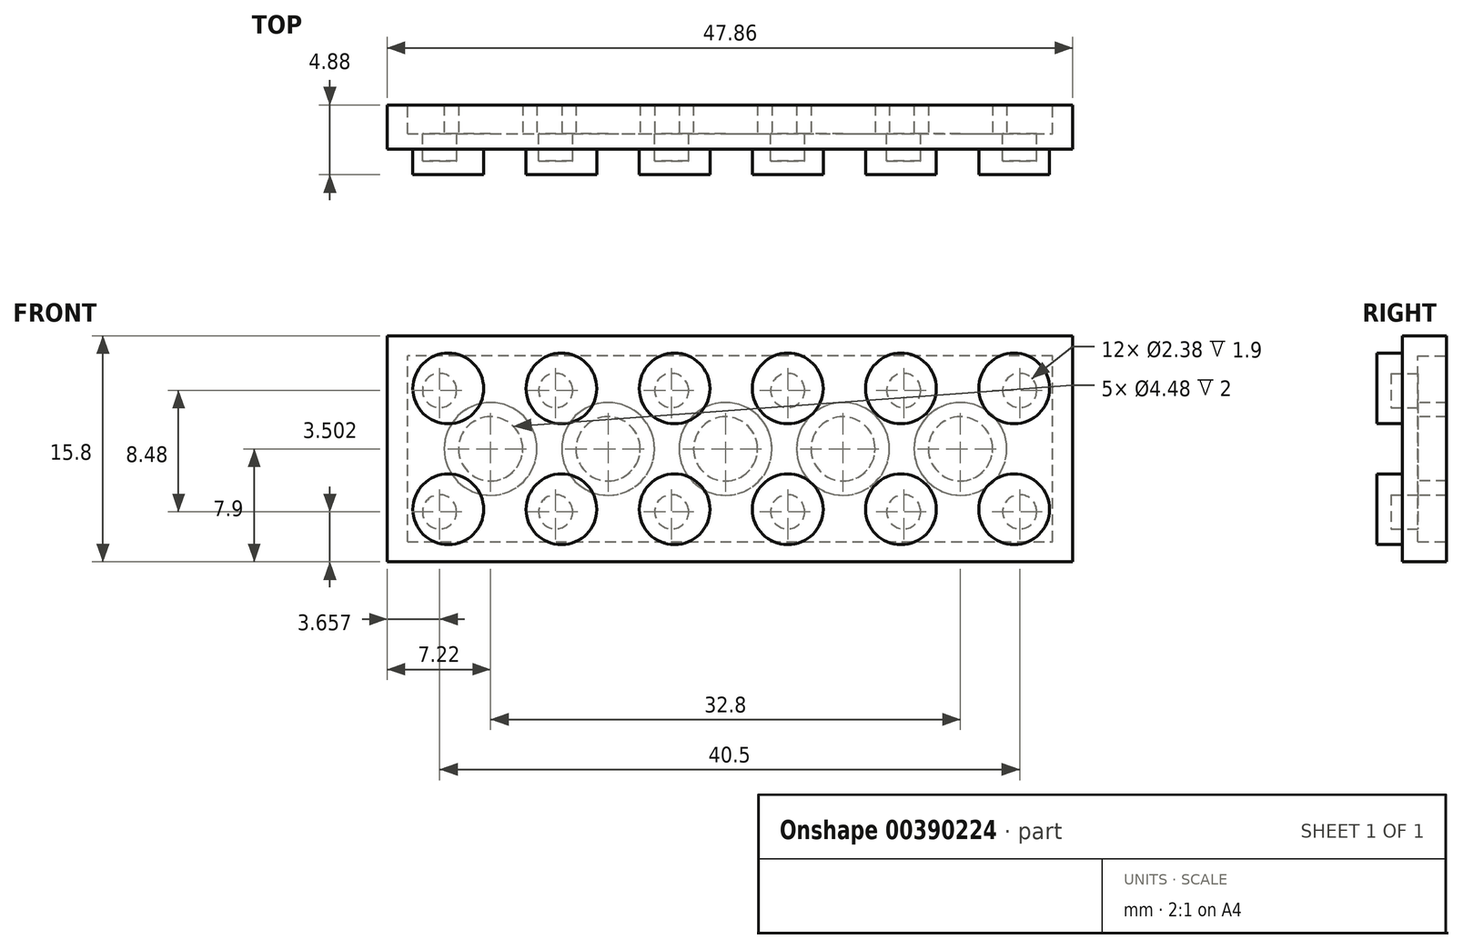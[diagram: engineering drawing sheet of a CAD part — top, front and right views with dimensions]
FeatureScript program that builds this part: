
annotation { "Feature Type Name" : "Feature", "Feature Type Description" : "" }
export const myFeature = defineFeature(function(context is Context, id is Id, definition is map)
    precondition{}
    {
        {
            var Q0;
            Q0=qCreatedBy(makeId("Front.planeOp"),FACE);
            var sketch = newSketch(context, id + "F0", { "sketchPlane" : qUnion([Q0])});
            skLineSegment(sketch, "E0", {"start": v(0, 0) * mm, "end": v(0, 15.8) * mm});
            skLineSegment(sketch, "E1", {"start": v(0, 15.8) * mm, "end": v(47.86, 15.8) * mm});
            skLineSegment(sketch, "E2", {"start": v(47.86, 15.8) * mm, "end": v(47.86, 0) * mm});
            skLineSegment(sketch, "E3", {"start": v(47.86, 0) * mm, "end": v(0, 0) * mm});
            skSolve(sketch);
        }
        {
            var Q0;
            Q0 = qSketchRegion(id + "F0", true);
            extrude(context, id + "F1", {"entities" : qUnion([Q0]), "depth" : 3.09 * mm});
        }
        {
            var Q0;
            Q0=makeQuery(id+"F1.opExtrude","CAP_FACE",FACE,{"disambiguationData":[OSD([sQuery(id+"F0.wireOp",EDGE,"E0"),sQuery(id+"F0.wireOp",EDGE,"E1"),sQuery(id+"F0.wireOp",EDGE,"E2"),sQuery(id+"F0.wireOp",EDGE,"E3")])],"isStart":false});
            var sketch = newSketch(context, id + "F2", { "sketchPlane" : qUnion([Q0])});
            skCircle(sketch, "E4", {"center": v(4.26, 12.12) * mm, "radius": 2.47 * mm});
            skCircle(sketch, "E5.1.0.0", {"center": v(12.16, 12.12) * mm, "radius": 2.47 * mm});
            skCircle(sketch, "E5.2.0.0", {"center": v(20.06, 12.12) * mm, "radius": 2.47 * mm});
            skCircle(sketch, "E5.3.0.0", {"center": v(27.96, 12.12) * mm, "radius": 2.47 * mm});
            skCircle(sketch, "E5.4.0.0", {"center": v(35.86, 12.12) * mm, "radius": 2.47 * mm});
            skCircle(sketch, "E5.5.0.0", {"center": v(43.76, 12.12) * mm, "radius": 2.47 * mm});
            skCircle(sketch, "E6", {"center": v(4.26, 3.67) * mm, "radius": 2.47 * mm});
            skCircle(sketch, "E7.1.0.0", {"center": v(12.16, 3.67) * mm, "radius": 2.47 * mm});
            skCircle(sketch, "E7.2.0.0", {"center": v(20.06, 3.67) * mm, "radius": 2.47 * mm});
            skCircle(sketch, "E7.3.0.0", {"center": v(27.96, 3.67) * mm, "radius": 2.47 * mm});
            skCircle(sketch, "E7.4.0.0", {"center": v(35.86, 3.67) * mm, "radius": 2.47 * mm});
            skCircle(sketch, "E7.5.0.0", {"center": v(43.76, 3.67) * mm, "radius": 2.47 * mm});
            skLineSegment(sketch, "E7.direction1", {"start": v(4.26, 3.67) * mm, "end": v(12.16, 3.67) * mm, "construction": true});
            skSolve(sketch);
        }
        {
            var Q0;
            Q0 = qSketchRegion(id + "F2", true);
            extrude(context, id + "F3", {"entities" : qUnion([Q0]), "operationType" : NewBodyOperationType.ADD, "depth" : 1.79 * mm});
        }
        {
            var Q0;
            Q0=makeQuery(id+"F1.opExtrude","CAP_FACE",FACE,{"disambiguationData":[OSD([sQuery(id+"F0.wireOp",EDGE,"E0"),sQuery(id+"F0.wireOp",EDGE,"E1"),sQuery(id+"F0.wireOp",EDGE,"E2"),sQuery(id+"F0.wireOp",EDGE,"E3")])],"isStart":true});
            var sketch = newSketch(context, id + "F4", { "sketchPlane" : qUnion([Q0])});
            skLineSegment(sketch, "E8.right", {"start": v(-1.42, 1.42) * mm, "end": v(-1.42, 14.38) * mm});
            skLineSegment(sketch, "E9", {"start": v(-1.42, 1.42) * mm, "end": v(-46.44, 1.42) * mm});
            skLineSegment(sketch, "E10", {"start": v(-46.44, 1.42) * mm, "end": v(-46.44, 14.38) * mm});
            skLineSegment(sketch, "E11", {"start": v(-46.44, 14.38) * mm, "end": v(-1.42, 14.38) * mm});
            skSolve(sketch);
        }
        {
            var Q0;
            Q0 = qSketchRegion(id + "F4", true);
            extrude(context, id + "F5", {"entities" : qUnion([Q0]), "operationType" : NewBodyOperationType.REMOVE, "oppositeDirection" : true, "depth" : 2 * mm});
        }
        {
            var Q0;
            Q0=makeQuery(id+"F5.boolean.opBoolean","COPY",FACE,{"derivedFrom":makeQuery(id+"F5.opExtrude","CAP_FACE",FACE,{"disambiguationData":[OSD([sQuery(id+"F4.wireOp",EDGE,"E8.right"),sQuery(id+"F4.wireOp",EDGE,"E9"),sQuery(id+"F4.wireOp",EDGE,"E10"),sQuery(id+"F4.wireOp",EDGE,"E11")])],"isStart":false})});
            var sketch = newSketch(context, id + "F6", { "sketchPlane" : qUnion([Q0])});
            skCircle(sketch, "E12", {"center": v(-40.02, 7.9) * mm, "radius": 3.24 * mm});
            skPoint(sketch, "E12.centerSnap0", {"position": v(-46.44, 7.9) * mm});
            skCircle(sketch, "E13.1.0.0", {"center": v(-31.82, 7.9) * mm, "radius": 3.24 * mm});
            skCircle(sketch, "E13.2.0.0", {"center": v(-23.62, 7.9) * mm, "radius": 3.24 * mm});
            skCircle(sketch, "E13.3.0.0", {"center": v(-15.42, 7.9) * mm, "radius": 3.24 * mm});
            skCircle(sketch, "E13.4.0.0", {"center": v(-7.22, 7.9) * mm, "radius": 3.24 * mm});
            skLineSegment(sketch, "E13.direction1", {"start": v(-40.02, 7.9) * mm, "end": v(-31.82, 7.9) * mm, "construction": true});
            skSolve(sketch);
        }
        {
            var Q0;
            Q0 = qSketchRegion(id + "F6", true);
            var Q1;
            Q1=makeQuery(id+"F1.opExtrude","CAP_FACE",FACE,{"disambiguationData":[OSD([sQuery(id+"F0.wireOp",EDGE,"E0"),sQuery(id+"F0.wireOp",EDGE,"E1"),sQuery(id+"F0.wireOp",EDGE,"E2"),sQuery(id+"F0.wireOp",EDGE,"E3")])],"isStart":true});
            extrude(context, id + "F7", {"entities" : qUnion([Q0]), "operationType" : NewBodyOperationType.ADD, "endBound" : BoundingType.UP_TO_SURFACE, "endBoundEntityFace" : qUnion([Q1]), "depth" : 25 * mm});
        }
        {
            var Q0;
            Q0=makeQuery(id+"F5.boolean.opBoolean","COPY",FACE,{"derivedFrom":makeQuery(id+"F5.opExtrude","CAP_FACE",FACE,{"disambiguationData":[OSD([sQuery(id+"F4.wireOp",EDGE,"E8.right"),sQuery(id+"F4.wireOp",EDGE,"E9"),sQuery(id+"F4.wireOp",EDGE,"E10"),sQuery(id+"F4.wireOp",EDGE,"E11")])],"isStart":false})});
            var sketch = newSketch(context, id + "F8", { "sketchPlane" : qUnion([Q0])});
            skCircle(sketch, "E14", {"center": v(-40.02, 7.9) * mm, "radius": 2.24 * mm});
            skCircle(sketch, "E15.1.0.0", {"center": v(-31.82, 7.9) * mm, "radius": 2.24 * mm});
            skCircle(sketch, "E15.2.0.0", {"center": v(-23.62, 7.9) * mm, "radius": 2.24 * mm});
            skCircle(sketch, "E15.3.0.0", {"center": v(-15.42, 7.9) * mm, "radius": 2.24 * mm});
            skCircle(sketch, "E15.4.0.0", {"center": v(-7.22, 7.9) * mm, "radius": 2.24 * mm});
            skLineSegment(sketch, "E15.direction1", {"start": v(-40.02, 7.9) * mm, "end": v(-31.82, 7.9) * mm, "construction": true});
            skSolve(sketch);
        }
        {
            var Q0;
            Q0 = qSketchRegion(id + "F8", true);
            extrude(context, id + "F9", {"entities" : qUnion([Q0]), "operationType" : NewBodyOperationType.REMOVE, "depth" : 2.2 * mm});
        }
        {
            var Q0;
            Q0=makeQuery(id+"F5.boolean.opBoolean","COPY",FACE,{"derivedFrom":makeQuery(id+"F5.opExtrude","CAP_FACE",FACE,{"disambiguationData":[OSD([sQuery(id+"F4.wireOp",EDGE,"E8.right"),sQuery(id+"F4.wireOp",EDGE,"E9"),sQuery(id+"F4.wireOp",EDGE,"E10"),sQuery(id+"F4.wireOp",EDGE,"E11")])],"isStart":false})});
            var sketch = newSketch(context, id + "F10", { "sketchPlane" : qUnion([Q0])});
            skCircle(sketch, "E16", {"center": v(-44.16, 11.98) * mm, "radius": 1.19 * mm});
            skCircle(sketch, "E17", {"center": v(-44.16, 3.5) * mm, "radius": 1.19 * mm});
            skCircle(sketch, "E18.1.0.0", {"center": v(-36.06, 11.98) * mm, "radius": 1.19 * mm});
            skCircle(sketch, "E18.1.0.1", {"center": v(-36.06, 3.5) * mm, "radius": 1.19 * mm});
            skCircle(sketch, "E18.2.0.0", {"center": v(-27.96, 11.98) * mm, "radius": 1.19 * mm});
            skCircle(sketch, "E18.2.0.1", {"center": v(-27.96, 3.5) * mm, "radius": 1.19 * mm});
            skCircle(sketch, "E18.3.0.0", {"center": v(-19.86, 11.98) * mm, "radius": 1.19 * mm});
            skCircle(sketch, "E18.3.0.1", {"center": v(-19.86, 3.5) * mm, "radius": 1.19 * mm});
            skCircle(sketch, "E18.4.0.0", {"center": v(-11.76, 11.98) * mm, "radius": 1.19 * mm});
            skCircle(sketch, "E18.4.0.1", {"center": v(-11.76, 3.5) * mm, "radius": 1.19 * mm});
            skCircle(sketch, "E18.5.0.0", {"center": v(-3.66, 11.98) * mm, "radius": 1.19 * mm});
            skCircle(sketch, "E18.5.0.1", {"center": v(-3.66, 3.5) * mm, "radius": 1.19 * mm});
            skLineSegment(sketch, "E18.direction1", {"start": v(-44.16, 11.98) * mm, "end": v(-36.06, 11.98) * mm, "construction": true});
            skSolve(sketch);
        }
        {
            var Q0;
            Q0 = qSketchRegion(id + "F10", true);
            extrude(context, id + "F11", {"entities" : qUnion([Q0]), "operationType" : NewBodyOperationType.REMOVE, "oppositeDirection" : true, "depth" : 1.9 * mm});
        }
    });
